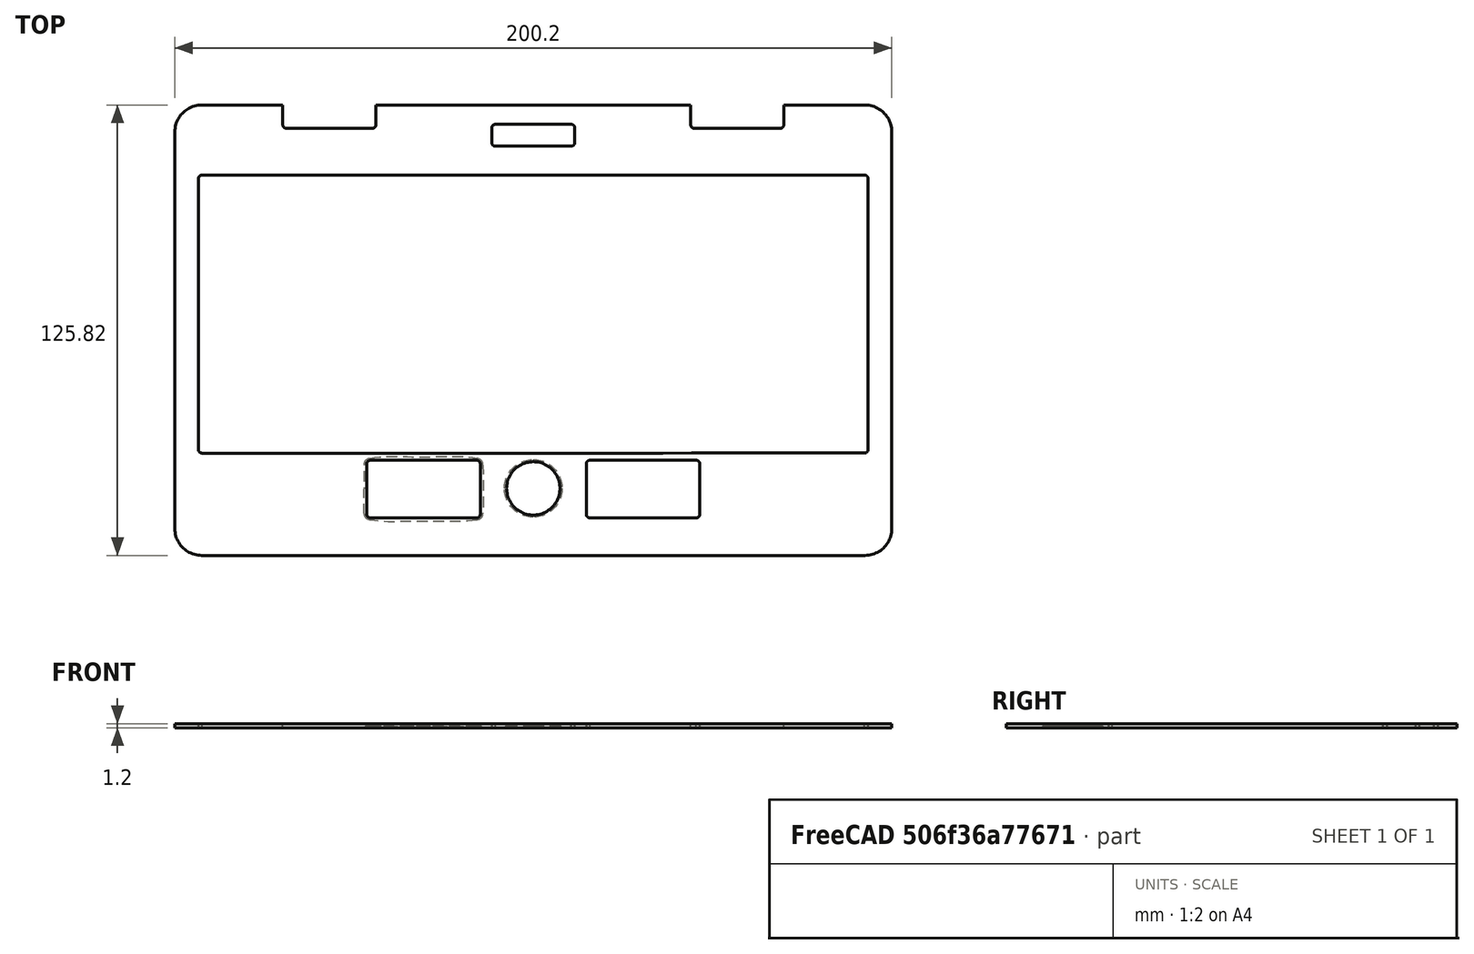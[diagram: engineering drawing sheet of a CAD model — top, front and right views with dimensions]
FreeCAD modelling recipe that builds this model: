
FCSTD DOCUMENT  (FreeCAD 2023.1024R14555 (Git shallow))
Label: pref-keyboard-bezel-freecad-recreate
License: All rights reserved
LicenseURL: https://en.wikipedia.org/wiki/All_rights_reserved
objects: Part::Feature×6, Part::Extrusion×6, Part::Chamfer×2, Part::MultiFuse×1, Part::Cut×1
note: 16 computed .brp shape members not serialized (recipe doc carries the construction recipe); baked Part::Feature solids carry a one-line shape summary decoded from their .brp

FEATURE [Part::Feature] path10041
  InvalidShape = false
  TreeRank = 7
  ValidateShape = false
  shape: bbox 200.2 x 125.8 x 2e-07 mm, 1 faces, 0 solids (baked)
FEATURE [Part::Feature] path10042
  InvalidShape = false
  TreeRank = 8
  ValidateShape = false
  shape: bbox 23.23 x 6.127 x 2e-07 mm, 1 faces, 0 solids (baked)
FEATURE [Part::Feature] path10043
  InvalidShape = false
  TreeRank = 9
  ValidateShape = false
  shape: bbox 187 x 77.69 x 2e-07 mm, 1 faces, 0 solids (baked)
FEATURE [Part::Feature] path10044
  InvalidShape = false
  TreeRank = 10
  ValidateShape = false
  shape: bbox 31.73 x 16.13 x 2e-07 mm, 1 faces, 0 solids (baked)
FEATURE [Part::Feature] path10045
  InvalidShape = false
  TreeRank = 11
  ValidateShape = false
  shape: bbox 31.73 x 16.13 x 2e-07 mm, 1 faces, 0 solids (baked)
FEATURE [Part::Feature] path10046
  InvalidShape = false
  TreeRank = 12
  ValidateShape = false
  shape: bbox 14.9 x 14.9 x 2e-07 mm, 1 faces, 0 solids (baked)
FEATURE [Part::Extrusion] Extrude
  AutoTaperInnerAngle = true
  Base = -> path10041
  Dir = (0,0,1)
  DirMode = 2
  FaceMakerClass = Part::FaceMakerBullseye
  InvalidShape = false
  LengthFwd = 1.2
  LengthRev = 0
  Linearize = true
  Solid = false
  Symmetric = false
  TaperInnerAngle = 0
  TaperInnerAngleRev = 0
  TreeRank = 24
  ValidateShape = false
FEATURE [Part::Extrusion] Extrude001
  AutoTaperInnerAngle = true
  Base = -> path10042
  Dir = (0,0,1)
  DirMode = 2
  FaceMakerClass = Part::FaceMakerBullseye
  InvalidShape = false
  LengthFwd = 1.2
  LengthRev = 0
  Linearize = true
  Solid = false
  Symmetric = false
  TaperInnerAngle = 0
  TaperInnerAngleRev = 0
  TreeRank = 28
  ValidateShape = false
FEATURE [Part::Extrusion] Extrude002
  AutoTaperInnerAngle = true
  Base = -> path10043
  Dir = (0,0,1)
  DirMode = 2
  FaceMakerClass = Part::FaceMakerBullseye
  InvalidShape = false
  LengthFwd = 1.2
  LengthRev = 0
  Linearize = true
  Solid = false
  Symmetric = false
  TaperInnerAngle = 0
  TaperInnerAngleRev = 0
  TreeRank = 30
  ValidateShape = false
FEATURE [Part::Extrusion] Extrude003
  AutoTaperInnerAngle = true
  Base = -> path10044
  Dir = (0,0,1)
  DirMode = 2
  FaceMakerClass = Part::FaceMakerBullseye
  InvalidShape = false
  LengthFwd = 1.2
  LengthRev = 0
  Linearize = true
  Solid = false
  Symmetric = false
  TaperInnerAngle = 0
  TaperInnerAngleRev = 0
  TreeRank = 25
  ValidateShape = false
FEATURE [Part::Extrusion] Extrude004
  AutoTaperInnerAngle = true
  Base = -> path10045
  Dir = (0,0,1)
  DirMode = 2
  FaceMakerClass = Part::FaceMakerBullseye
  InvalidShape = false
  LengthFwd = 1.2
  LengthRev = 0
  Linearize = true
  Solid = false
  Symmetric = false
  TaperInnerAngle = 0
  TaperInnerAngleRev = 0
  TreeRank = 26
  ValidateShape = false
FEATURE [Part::Extrusion] Extrude005
  AutoTaperInnerAngle = true
  Base = -> path10046
  Dir = (0,0,1)
  DirMode = 2
  FaceMakerClass = Part::FaceMakerBullseye
  InvalidShape = false
  LengthFwd = 1.2
  LengthRev = 0
  Linearize = true
  Solid = false
  Symmetric = false
  TaperInnerAngle = 0
  TaperInnerAngleRev = 0
  TreeRank = 27
  ValidateShape = false
FEATURE [Part::MultiFuse] Fusion
  InvalidShape = false
  Shapes = -> [Extrude003,Extrude004,Extrude005,Extrude001,Extrude002]
  TreeRank = 31
  ValidateShape = false
FEATURE [Part::Cut] Cut
  Base = -> Extrude
  InvalidShape = false
  Tool = -> Fusion
  TreeRank = 32
  ValidateShape = false
FEATURE [Part::Chamfer] Chamfer
  Base = -> Cut
  EdgeLinks = -> Cut [Edge36,Edge37,Edge38,Edge39]
  Edges = 4 edges r=0.6: [Edge36,Edge37,Edge38,Edge39]
  InvalidShape = false
  TreeRank = 33
  ValidateShape = false
FEATURE [Part::Chamfer] Chamfer001
  Base = -> Chamfer
  EdgeLinks = -> Chamfer [Edge25,Edge26,Edge27,Edge28,Edge29,Edge30,Edge31,Edge32]
  Edges = 8 edges r=0.4: [Edge25,Edge26,Edge27,Edge28,Edge29,Edge30,Edge31,Edge32]
  InvalidShape = false
  TreeRank = 34
  ValidateShape = false
